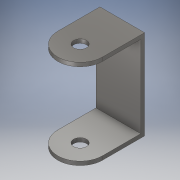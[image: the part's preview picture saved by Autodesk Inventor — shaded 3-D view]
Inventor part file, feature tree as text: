
AUTODESK INVENTOR PART (.ipt)
format: ipt  version: 2019 (Build 230136000, 136)  size: 139,264 bytes
history: native  units: mm
features: extrude x3, sketch x3, projected_geometry x2
ambient origin geometry x8: Origin, YZ Plane, XZ Plane, XY Plane, X Axis, Y Axis, Z Axis, Center Point
bodies: Solid1 (feature_tree)
feature tree (8):
  extrude  "Extrusion1"  Depth=35.0mm
  extrude  "Extrusion4"  Depth=10.1mm
  extrude  "Extrusion5"  Depth=3.0mm
  sketch  "Sketch1"  dims[d0=35.0mm d1=33.0mm]
  sketch  "Sketch5"  dims[d2=90.0deg d3=10.1mm]
  projected_geometry  "Projected Loop3"
  sketch  "Sketch6"  dims[d4=3.0mm d5=0.0mm d11=3.0mm d12=70.0mm d13=0.0mm d14=3.0mm d15=0.0mm]
  projected_geometry  "Projected Loop4"
